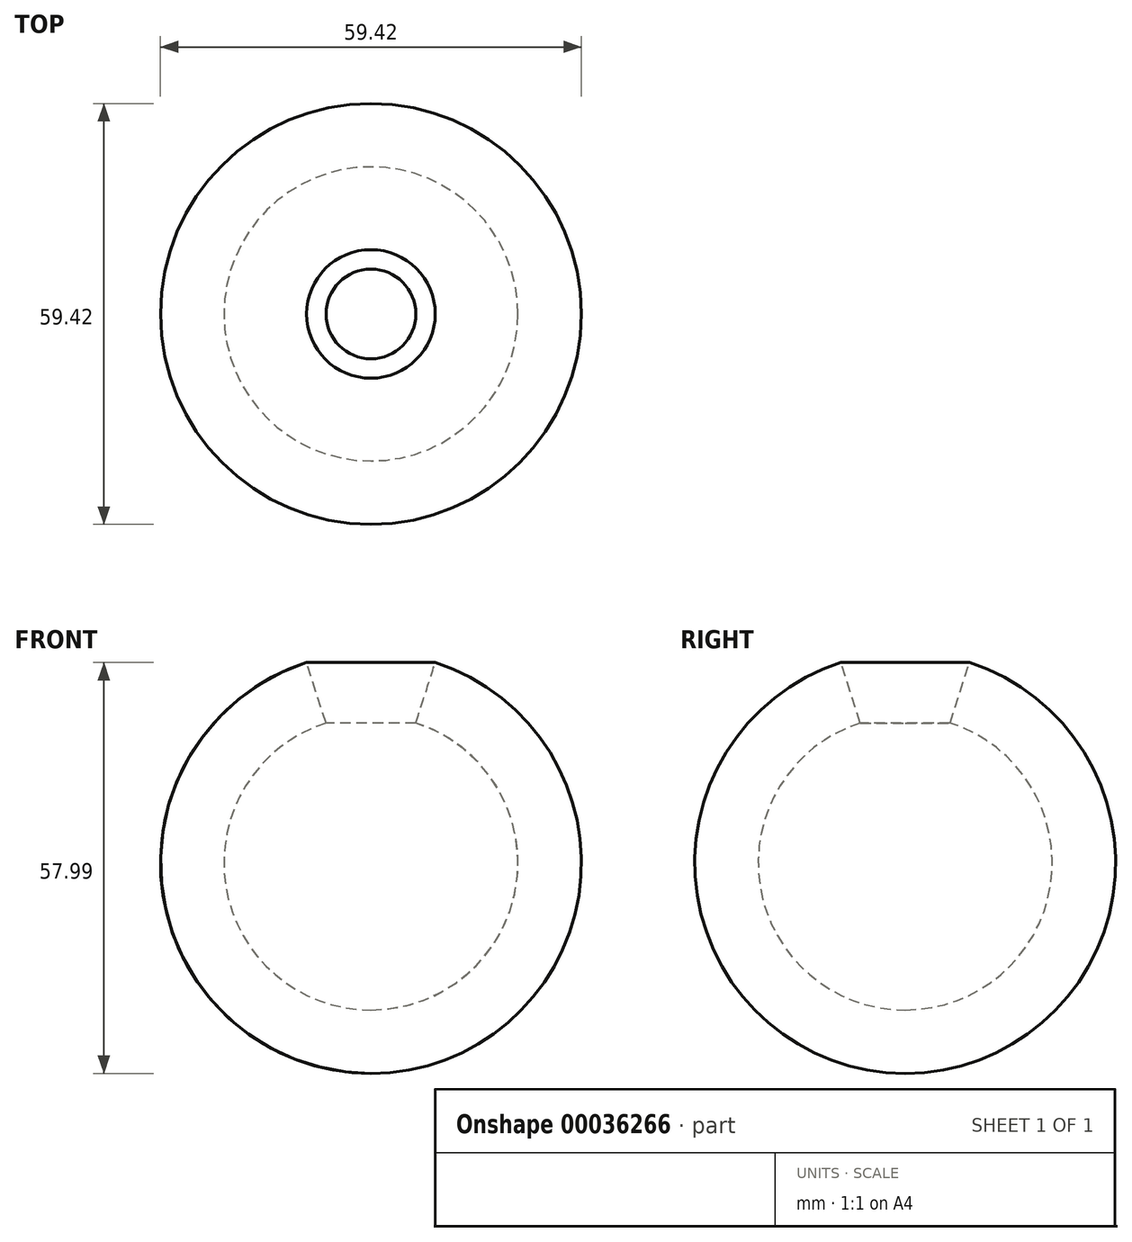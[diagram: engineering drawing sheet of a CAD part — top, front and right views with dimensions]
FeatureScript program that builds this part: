
annotation { "Feature Type Name" : "Feature", "Feature Type Description" : "" }
export const myFeature = defineFeature(function(context is Context, id is Id, definition is map)
    precondition{}
    {
        {
            var Q0;
            Q0=qCreatedBy(makeId("Front.planeOp"),FACE);
            var sketch = newSketch(context, id + "F0", { "sketchPlane" : qUnion([Q0])});
            skArc(sketch, "E0", {"start": v(0, -41.5) * mm, "mid": v(20.5, -23.96) * mm, "end": v(6.34, -1) * mm});
            skArc(sketch, "E1.0", {"start": v(0, -50.46) * mm, "mid": v(29.35, -25.34) * mm, "end": v(9.07, 7.53) * mm});
            skLineSegment(sketch, "E2", {"start": v(0, -41.5) * mm, "end": v(0, -50.46) * mm});
            skLineSegment(sketch, "E3", {"start": v(9.07, 7.53) * mm, "end": v(6.34, -1) * mm});
            skSolve(sketch);
        }
        {
            var Q0;
            Q0 = qSketchRegion(id + "F0", true);
            var Q1;
            Q1=sQuery(id+"F0.wireOp",EDGE,"E2");
            revolve(context, id + "F1", {"entities" : qUnion([Q0]), "axis" : qUnion([Q1]), "revolveType" : RevolveType.FULL});
        }
    });
